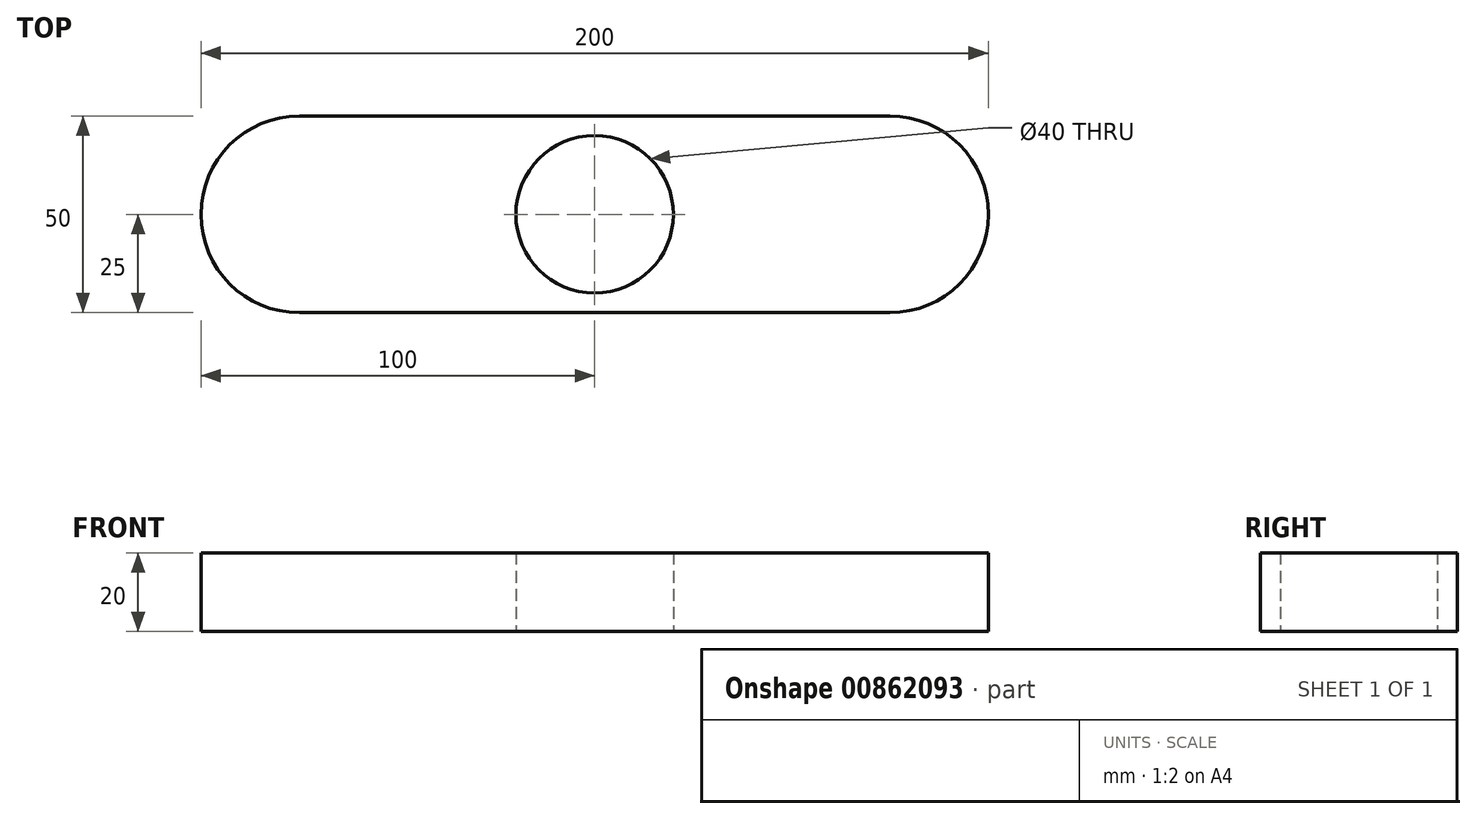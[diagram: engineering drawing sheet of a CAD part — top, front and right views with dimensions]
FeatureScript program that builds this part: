
annotation { "Feature Type Name" : "Feature", "Feature Type Description" : "" }
export const myFeature = defineFeature(function(context is Context, id is Id, definition is map)
    precondition{}
    {
        {
            var Q0;
            Q0=qCreatedBy(makeId("Top.planeOp"),FACE);
            var sketch = newSketch(context, id + "F0", { "sketchPlane" : qUnion([Q0])});
            skLineSegment(sketch, "E0.bottom", {"start": v(0, 50) * mm, "end": v(200, 50) * mm});
            skLineSegment(sketch, "E0.top", {"start": v(0, 0) * mm, "end": v(200, 0) * mm});
            skLineSegment(sketch, "E0.left", {"start": v(0, 50) * mm, "end": v(0, 0) * mm});
            skLineSegment(sketch, "E0.right", {"start": v(200, 50) * mm, "end": v(200, 0) * mm});
            skCircle(sketch, "E1", {"center": v(100, 25) * mm, "radius": 20 * mm});
            skLineSegment(sketch, "E2", {"start": v(0, 50) * mm, "end": v(200, 0) * mm, "construction": true});
            skSolve(sketch);
        }
        {
            var Q0;
            Q0=makeQuery(id+"F0.imprint","IMPRINT",FACE,{"disambiguationData":[TD([[makeQuery(id+"F0.imprint","IMPRINT",EDGE,{"derivedFrom":sQuery(id+"F0.wireOp",EDGE,"E0.bottom")}),-1.0]])]});
            extrude(context, id + "F1", {"entities" : qUnion([Q0]), "depth" : 20 * mm, "offsetDistance" : 25.4 * mm});
        }
        {
            var Q0;
            Q0=makeQuery(id+"F1.opExtrude","SWEPT_EDGE",EDGE,{"disambiguationData":[OSD([sQuery(id+"F0.wireOp",EDGE,"E0.top"),sQuery(id+"F0.wireOp",EDGE,"E0.right")])]});
            var Q1;
            Q1=makeQuery(id+"F1.opExtrude","SWEPT_EDGE",EDGE,{"disambiguationData":[OSD([sQuery(id+"F0.wireOp",EDGE,"E0.bottom"),sQuery(id+"F0.wireOp",EDGE,"E0.left")])]});
            var Q2;
            Q2=makeQuery(id+"F1.opExtrude","SWEPT_EDGE",EDGE,{"disambiguationData":[OSD([sQuery(id+"F0.wireOp",EDGE,"E0.top"),sQuery(id+"F0.wireOp",EDGE,"E0.left")])]});
            var Q3;
            Q3=makeQuery(id+"F1.opExtrude","SWEPT_EDGE",EDGE,{"disambiguationData":[OSD([sQuery(id+"F0.wireOp",EDGE,"E0.bottom"),sQuery(id+"F0.wireOp",EDGE,"E0.right")])]});
            fillet(context, id + "F2", {"entities" : qUnion([Q0, Q1, Q2, Q3]), "radius" : 25 * mm, "tangentPropagation" : true, "allowEdgeOverflow" : false});
        }
    });
